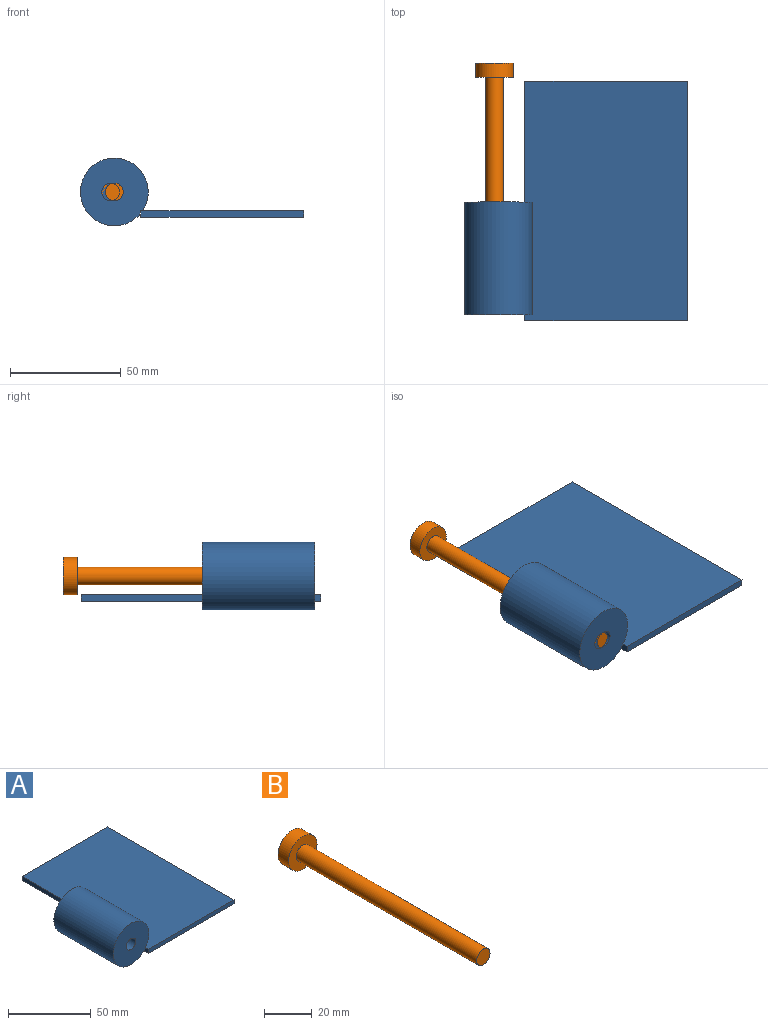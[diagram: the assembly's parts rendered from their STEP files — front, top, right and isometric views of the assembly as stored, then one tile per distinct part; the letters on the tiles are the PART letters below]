
ASSEMBLY  parts=2 mates=1
PART A: 10 faces, bbox 100.7x108.3x30.6 mm
  f0: plane 108.27x3.05mm, normal (-1,0,0), area 279.1mm2, adj f1,f3,f4,f5,f6,f7,f8
  f1: plane 73.4x3.05mm, normal (0,-1,0), area 223.7mm2, adj f0,f2,f4,f5
  f2: plane 108.27x3.05mm, normal (1,0,0), area 330mm2, adj f1,f3,f4,f5
  f3: plane 73.4x3.05mm, normal (0,1,0), area 223.7mm2, adj f0,f2,f4,f5
  f4: plane 108.27x73.4mm, normal (0,0,1), area 7909.5mm2, adj f0,f1,f2,f3,f6,f7,f8
  f5: plane 108.27x73.4mm, normal (0,0,-1), area 7946.5mm2, adj f0,f1,f2,f3
  f6: cylinder r=15.28mm len=50.8mm, axis (0,1,0), area 4812.8mm2, adj f0,f4,f7,f8
  f7: plane 30.55x30.55mm, normal (0,-1,0), area 681.7mm2, adj f0,f4,f6,f9
  f8: plane 30.55x30.55mm, normal (0,1,0), area 681.7mm2, adj f0,f4,f6,f9
  f9: cylinder r=4.03mm len=50.8mm, axis (0,-1,0), area 1286.1mm2, adj f7,f8
PART B: 5 faces, bbox 16.8x113.5x16.8 mm
  f0: cylinder r=4mm len=107.19mm, axis (0,1,0), area 2692.8mm2, adj f1,f4
  f1: plane 8x8mm, normal (0,-1,0), area 50.2mm2, adj f0
  f2: cylinder r=8.42mm len=16.84mm, axis (0,-1,0), area 335.9mm2, adj f3,f4
  f3: plane 16.84x16.84mm, normal (0,1,0), area 222.7mm2, adj f2
  f4: plane 16.84x16.84mm, normal (0,-1,0), area 172.5mm2, adj f0,f2
PLACE A rot(axis=(0.75,-0.02,0.66),0deg) t=(0.26,44.77,6.01)mm
PLACE B rot(axis=(0.16,0.98,0.15),0deg) t=(-19,101.16,17.52)mm
MATE pin_slot B.f0 <-> A.f6  axis (0,-1,0) through (-19,-6.03,17.52)mm
